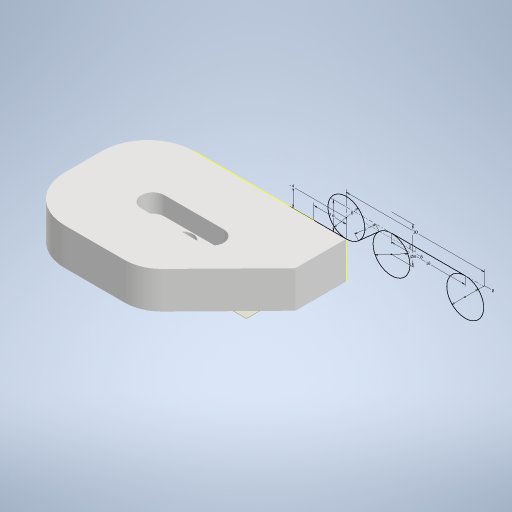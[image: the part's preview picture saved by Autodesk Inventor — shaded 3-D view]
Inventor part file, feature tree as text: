
AUTODESK INVENTOR PART (.ipt)
format: ipt  version: 2024 (Build 280153000, 153)  size: 301,056 bytes
history: native  units: mm
features: sketch x4, other x4, extrude x3, plane x1, fillet x1, reference x1, projected_geometry x1
ambient origin geometry x8: Origin, YZ Plane, XZ Plane, XY Plane, X Axis, Y Axis, Z Axis, Center Point
bodies: Solid1 (feature_tree)
feature tree (15):
  plane  "Work Plane1"
  extrude  "Extrusion1"  Depth=28.0mm
  extrude  "Extrusion2"  Depth=5.0mm
  fillet  "Fillet1"  Radius=5.0mm
  extrude  "Extrusion3"  Depth=10.0mm
  sketch  "Sketch4"  dims[d9=23.0mm d10=16.0mm d11=90.0deg d12=0.0mm d13=8.0mm d14=11.0mm d15=0.0mm d16=0.0mm d17=7.0mm d18=8.0mm d19=4.0mm d20=6.0mm d21=30.0mm d23=1.0mm d24=6.0mm d25=8.0mm d26=8.0mm d27=16.0mm d28=8.0mm]
  sketch  "Sketch1"  dims[d0=43.0mm d1=28.0mm]
  reference  "Reference1"
  sketch  "Sketch2"  dims[d2=8.0mm d3=0.0mm d4=5.0mm d5=5.0mm]
  sketch  "Sketch3"  dims[d6=4.0mm d7=0.0mm d8=10.0mm]
  projected_geometry  "Projected Loop1"
  other  "<userpath> windows\Documents\Inventor\Robotska_roka\Assembly4.iam"
  other  "Assembly4.iam"
  other  "SG90 - Micro Servo 9g - Tower Pro:2"
  other  "SG90 - Micro Servo 9g - Tower Pro.3"
